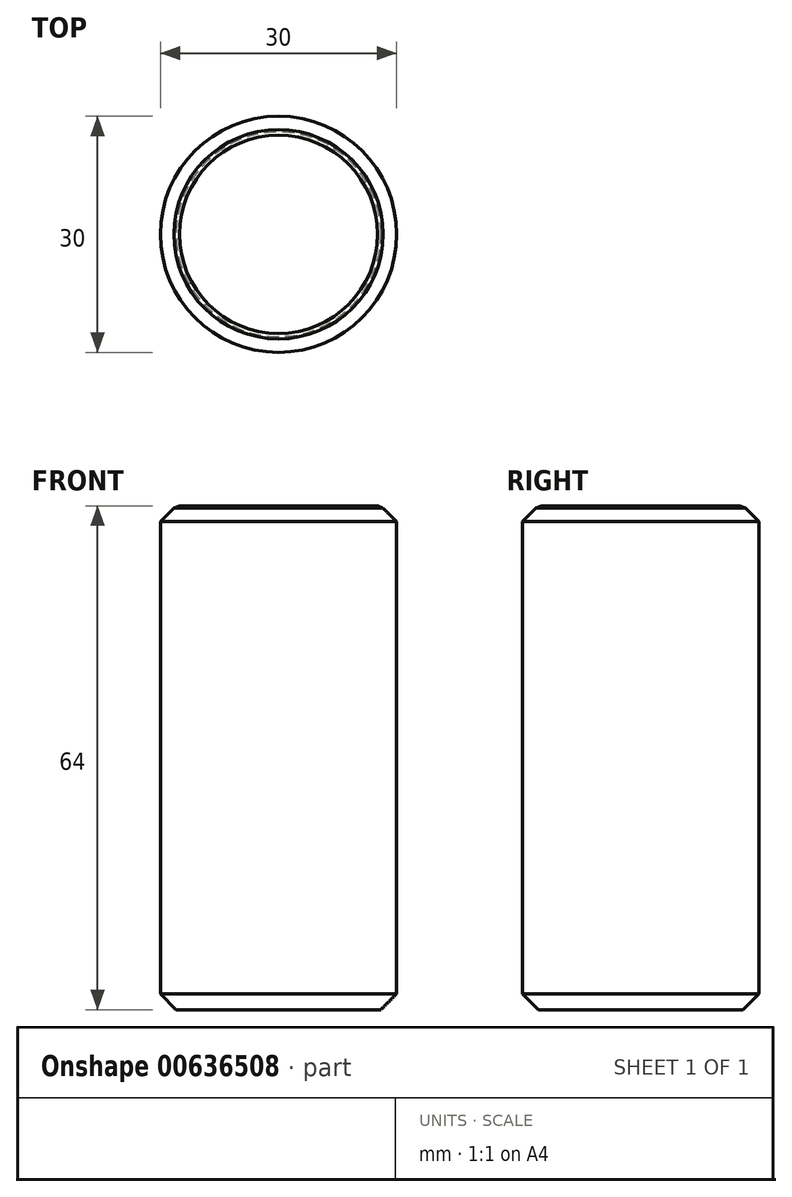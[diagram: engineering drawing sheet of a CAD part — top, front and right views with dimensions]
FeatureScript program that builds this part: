
annotation { "Feature Type Name" : "Feature", "Feature Type Description" : "" }
export const myFeature = defineFeature(function(context is Context, id is Id, definition is map)
    precondition{}
    {
        {
            var Q0;
            Q0=qCreatedBy(makeId("Top.planeOp"),FACE);
            var sketch = newSketch(context, id + "F0", { "sketchPlane" : qUnion([Q0])});
            skCircle(sketch, "E0", {"center": v(95, 0) * mm, "radius": 15 * mm});
            skSolve(sketch);
        }
        {
            var Q0;
            Q0=makeQuery(id+"F0.imprint","IMPRINT",FACE,{"disambiguationData":[TD([[makeQuery(id+"F0.imprint","IMPRINT",EDGE,{"derivedFrom":sQuery(id+"F0.wireOp",EDGE,"E0")}),1.0]])]});
            extrude(context, id + "F1", {"entities" : qUnion([Q0]), "endBound" : BoundingType.SYMMETRIC, "depth" : 64 * mm, "offsetDistance" : 25 * mm});
        }
        {
            var Q0;
            Q0=makeQuery(id+"F1.opExtrude","CAP_EDGE",EDGE,{"disambiguationData":[OSD([sQuery(id+"F0.wireOp",EDGE,"E0")])],"isStart":false});
            var Q1;
            Q1=makeQuery(id+"F1.opExtrude","CAP_EDGE",EDGE,{"disambiguationData":[OSD([sQuery(id+"F0.wireOp",EDGE,"E0")])],"isStart":true});
            chamfer(context, id + "F2", {"entities" : qUnion([Q0, Q1]), "width" : 2 * mm, "tangentPropagation" : true});
        }
        {
            var Q0;
            {var subQ0=sQuery(id+"F0.wireOp",EDGE,"E0");Q0=makeQuery(id+"F2.opChamfer","BLEND_EDGE",EDGE,{"blendedFrom":[makeQuery(id+"F1.opExtrude","CAP_EDGE",EDGE,{"disambiguationData":[OSD([subQ0])],"isStart":false}),makeQuery(id+"F1.opExtrude","CAP_FACE",FACE,{"disambiguationData":[OSD([subQ0])],"isStart":false})],"blendedInto":[makeQuery(id+"F1.opExtrude","CAP_FACE",FACE,{"disambiguationData":[OSD([subQ0])],"isStart":false})]});}
            chamfer(context, id + "F3", {"entities" : qUnion([Q0]), "width" : 1 * mm, "tangentPropagation" : true});
        }
        {
            var Q0;
            Q0=makeQuery(id+"F1.opExtrude","SWEPT_BODY",BODY,{"disambiguationData":[OSD([sQuery(id+"F0.wireOp",EDGE,"E0")])]});
            var Q1;
            Q1=qCreatedBy(makeId("Top.planeOp"),FACE);
            transform(context, id + "F4", {"entities" : qUnion([Q0]), "transformType" : TransformType.TRANSLATION_DISTANCE, "transformDirection" : qUnion([Q1]), "distance" : 40 * mm, "makeCopy" : false});
        }
    });
